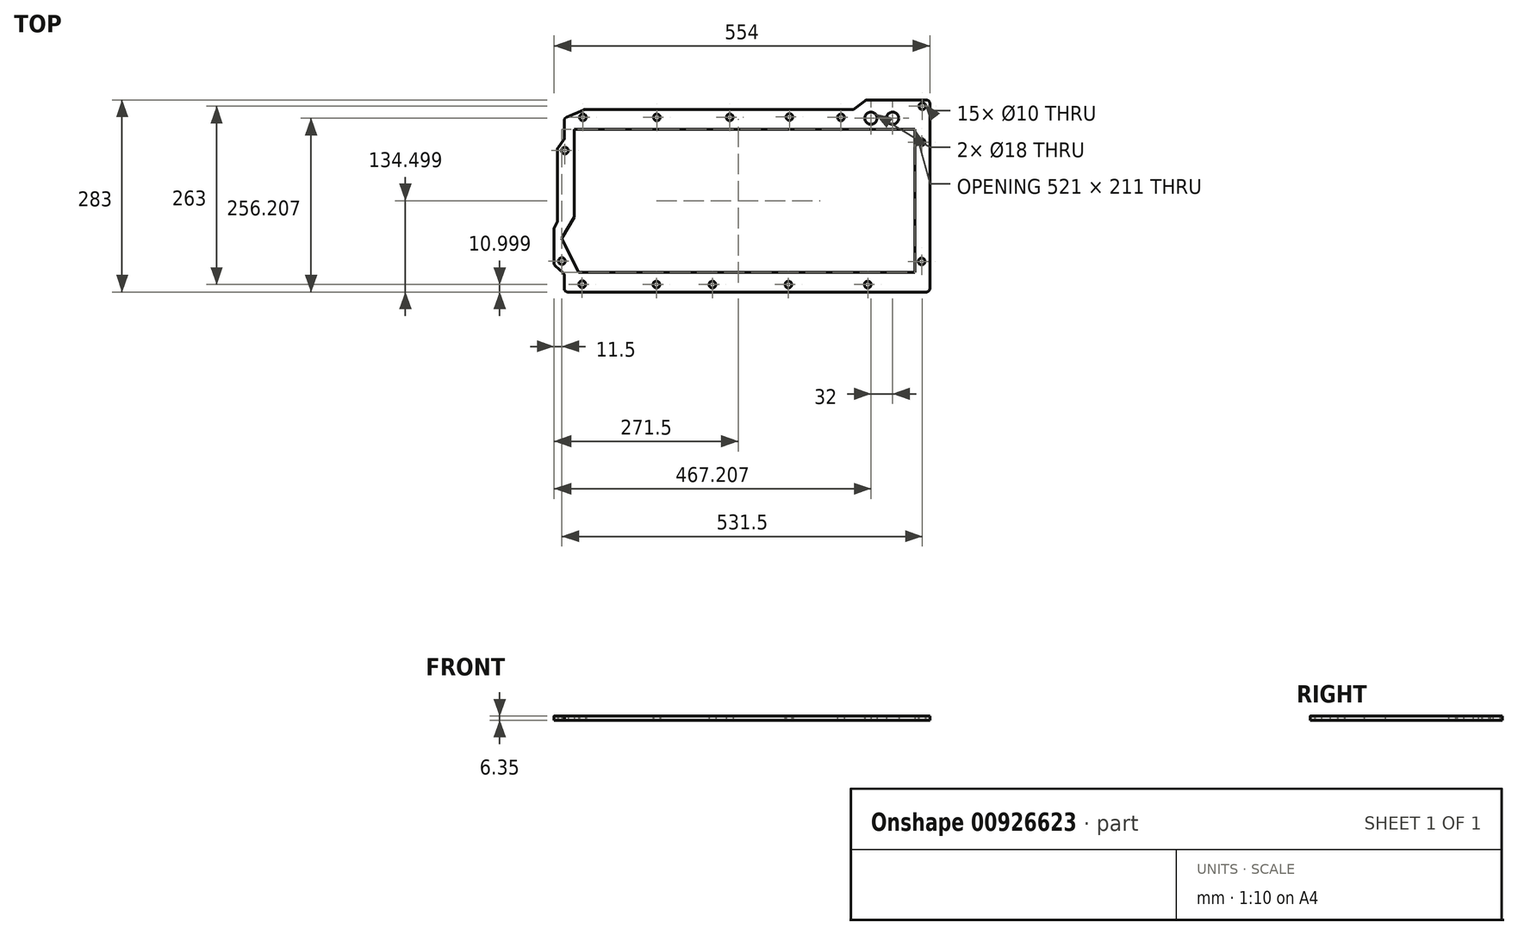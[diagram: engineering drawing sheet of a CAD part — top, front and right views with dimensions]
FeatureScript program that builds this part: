
annotation { "Feature Type Name" : "Feature", "Feature Type Description" : "" }
export const myFeature = defineFeature(function(context is Context, id is Id, definition is map)
    precondition{}
    {
        {
            var Q0;
            Q0=qCreatedBy(makeId("Top.planeOp"),FACE);
            var sketch = newSketch(context, id + "F0", { "sketchPlane" : qUnion([Q0])});
            skLineSegment(sketch, "E0", {"start": v(-236.29, -106.2) * mm, "end": v(-261.29, -56.2) * mm});
            skLineSegment(sketch, "E1", {"start": v(-261.29, -56.2) * mm, "end": v(-242.29, -25.2) * mm});
            skLineSegment(sketch, "E2", {"start": v(-242.29, -25.2) * mm, "end": v(-242.29, 104.8) * mm});
            skCircle(sketch, "E3", {"center": v(150.71, 122.3) * mm, "radius": 5 * mm});
            skCircle(sketch, "E4", {"center": v(74.71, 122.8) * mm, "radius": 5 * mm});
            skCircle(sketch, "E5", {"center": v(-13.29, 122.3) * mm, "radius": 5 * mm});
            skCircle(sketch, "E6", {"center": v(-120.79, 122.3) * mm, "radius": 5 * mm});
            skCircle(sketch, "E7", {"center": v(-229.79, 122.3) * mm, "radius": 5 * mm});
            skCircle(sketch, "E8", {"center": v(-256.29, 73.3) * mm, "radius": 5 * mm});
            skCircle(sketch, "E9", {"center": v(-260.79, -89.7) * mm, "radius": 5 * mm});
            skCircle(sketch, "E10", {"center": v(-230.79, -123.7) * mm, "radius": 5 * mm});
            skCircle(sketch, "E11", {"center": v(-121.29, -124.2) * mm, "radius": 5 * mm});
            skCircle(sketch, "E12", {"center": v(-38.79, -124.2) * mm, "radius": 5 * mm});
            skCircle(sketch, "E13", {"center": v(73.21, -124.2) * mm, "radius": 5 * mm});
            skCircle(sketch, "E14", {"center": v(190.21, -124.2) * mm, "radius": 5 * mm});
            skCircle(sketch, "E15", {"center": v(269.71, -90.2) * mm, "radius": 5 * mm});
            skCircle(sketch, "E16", {"center": v(269.71, 85.8) * mm, "radius": 5 * mm});
            skCircle(sketch, "E17", {"center": v(270.71, 138.8) * mm, "radius": 5 * mm});
            skCircle(sketch, "E18", {"center": v(194.92, 121.02) * mm, "radius": 9 * mm});
            skCircle(sketch, "E19", {"center": v(226.92, 121.02) * mm, "radius": 9 * mm});
            skLineSegment(sketch, "E20", {"start": v(-242.29, 104.8) * mm, "end": v(259.71, 104.8) * mm});
            skLineSegment(sketch, "E21", {"start": v(259.71, 104.8) * mm, "end": v(259.71, -106.2) * mm});
            skLineSegment(sketch, "E22", {"start": v(259.71, -106.2) * mm, "end": v(-236.29, -106.2) * mm});
            skLineSegment(sketch, "E23", {"start": v(189, 147.8) * mm, "end": v(276.71, 147.8) * mm});
            skLineSegment(sketch, "E24", {"start": v(281.71, 142.8) * mm, "end": v(281.71, -130.2) * mm});
            skLineSegment(sketch, "E25", {"start": v(185.93, 146.76) * mm, "end": v(170.64, 134.86) * mm});
            skLineSegment(sketch, "E26", {"start": v(167.57, 133.8) * mm, "end": v(-226.7, 133.8) * mm});
            skLineSegment(sketch, "E27", {"start": v(-228.7, 133.39) * mm, "end": v(-254.3, 122.12) * mm});
            skLineSegment(sketch, "E28", {"start": v(-257.29, 117.55) * mm, "end": v(-257.29, 91.51) * mm});
            skLineSegment(sketch, "E29", {"start": v(-258.33, 88.46) * mm, "end": v(-266.25, 78.16) * mm});
            skLineSegment(sketch, "E30", {"start": v(-267.29, 75.1) * mm, "end": v(-267.29, -30.01) * mm});
            skLineSegment(sketch, "E31", {"start": v(-267.82, -32.25) * mm, "end": v(-271.76, -40.13) * mm});
            skLineSegment(sketch, "E32", {"start": v(-272.29, -42.37) * mm, "end": v(-272.29, -92.9) * mm});
            skLineSegment(sketch, "E33", {"start": v(-270.56, -96.69) * mm, "end": v(-259.02, -106.7) * mm});
            skLineSegment(sketch, "E34", {"start": v(276.71, -135.2) * mm, "end": v(-252.29, -135.2) * mm});
            skLineSegment(sketch, "E35", {"start": v(-257.29, -110.47) * mm, "end": v(-257.29, -130.2) * mm});
            skPoint(sketch, "E36.visualSharp", {"position": v(-227.74, 133.8) * mm});
            skArc(sketch, "E36.filletArc", {"start": v(-226.7, 133.8) * mm, "mid": v(-227.72, 133.7) * mm, "end": v(-228.7, 133.39) * mm});
            skPoint(sketch, "E37.visualSharp", {"position": v(-257.29, 120.8) * mm});
            skArc(sketch, "E37.filletArc", {"start": v(-254.3, 122.12) * mm, "mid": v(-256.48, 120.28) * mm, "end": v(-257.29, 117.55) * mm});
            skPoint(sketch, "E38.visualSharp", {"position": v(-257.29, 89.8) * mm});
            skArc(sketch, "E38.filletArc", {"start": v(-258.33, 88.46) * mm, "mid": v(-257.56, 89.9) * mm, "end": v(-257.29, 91.51) * mm});
            skPoint(sketch, "E39.visualSharp", {"position": v(-267.29, 76.8) * mm});
            skArc(sketch, "E39.filletArc", {"start": v(-266.25, 78.16) * mm, "mid": v(-267.02, 76.72) * mm, "end": v(-267.29, 75.1) * mm});
            skPoint(sketch, "E40.visualSharp", {"position": v(-267.29, -31.2) * mm});
            skArc(sketch, "E40.filletArc", {"start": v(-267.82, -32.25) * mm, "mid": v(-267.42, -31.16) * mm, "end": v(-267.29, -30.01) * mm});
            skPoint(sketch, "E41.visualSharp", {"position": v(-272.29, -41.2) * mm});
            skArc(sketch, "E41.filletArc", {"start": v(-271.76, -40.13) * mm, "mid": v(-272.16, -41.22) * mm, "end": v(-272.29, -42.37) * mm});
            skPoint(sketch, "E42.visualSharp", {"position": v(-272.29, -95.2) * mm});
            skArc(sketch, "E42.filletArc", {"start": v(-272.29, -92.9) * mm, "mid": v(-271.84, -94.98) * mm, "end": v(-270.56, -96.69) * mm});
            skPoint(sketch, "E43.visualSharp", {"position": v(-257.29, -108.2) * mm});
            skArc(sketch, "E43.filletArc", {"start": v(-257.29, -110.47) * mm, "mid": v(-257.74, -108.4) * mm, "end": v(-259.02, -106.7) * mm});
            skPoint(sketch, "E44.visualSharp", {"position": v(-257.29, -135.2) * mm});
            skArc(sketch, "E44.filletArc", {"start": v(-257.29, -130.2) * mm, "mid": v(-255.83, -133.73) * mm, "end": v(-252.29, -135.2) * mm});
            skPoint(sketch, "E45.visualSharp", {"position": v(281.71, -135.2) * mm});
            skArc(sketch, "E45.filletArc", {"start": v(276.71, -135.2) * mm, "mid": v(280.25, -133.73) * mm, "end": v(281.71, -130.2) * mm});
            skPoint(sketch, "E46.visualSharp", {"position": v(281.71, 147.8) * mm});
            skArc(sketch, "E46.filletArc", {"start": v(281.71, 142.8) * mm, "mid": v(280.25, 146.34) * mm, "end": v(276.71, 147.8) * mm});
            skPoint(sketch, "E47.visualSharp", {"position": v(187.28, 147.8) * mm});
            skArc(sketch, "E47.filletArc", {"start": v(189, 147.8) * mm, "mid": v(187.37, 147.54) * mm, "end": v(185.93, 146.76) * mm});
            skPoint(sketch, "E48.visualSharp", {"position": v(169.28, 133.8) * mm});
            skArc(sketch, "E48.filletArc", {"start": v(167.57, 133.8) * mm, "mid": v(169.19, 134.08) * mm, "end": v(170.64, 134.86) * mm});
            skSolve(sketch);
        }
        {
            var Q0;
            Q0=makeQuery(id+"F0.imprint","IMPRINT",FACE,{"disambiguationData":[TD([[makeQuery(id+"F0.imprint","IMPRINT",EDGE,{"derivedFrom":sQuery(id+"F0.wireOp",EDGE,"E0")}),1.0]])]});
            extrude(context, id + "F1", {"entities" : qUnion([Q0]), "depth" : 6.35 * mm, "offsetDistance" : 25.4 * mm});
        }
    });
